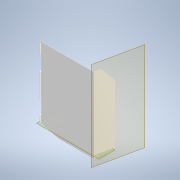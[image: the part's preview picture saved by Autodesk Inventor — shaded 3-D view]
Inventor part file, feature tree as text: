
AUTODESK INVENTOR PART (.ipt)
format: ipt  version: 2021 (Build 250183000, 183)  size: 199,168 bytes
history: native  units: mm
features: sketch x7, extrude x6, fillet x5, plane x2, other x2, hole x1
ambient origin geometry x8: Origin, YZ Plane, XZ Plane, XY Plane, X Axis, Y Axis, Z Axis, Center Point
bodies: Solid1 (feature_tree)
feature tree (23):
  extrude  "Extrusion1"  Depth=1300.0mm
  extrude  "Extrusion2"  Depth=20.0mm
  extrude  "Extrusion3"  Depth=2.5mm
  plane  "Work Plane1"
  extrude  "Extrusion4"  Depth=650.0mm
  fillet  "Fillet1"  Radius=550.0mm
  fillet  "Fillet2"  Radius=200.0mm
  fillet  "Fillet3"  Radius=200.0mm
  plane  "Work Plane2"
  extrude  "Extrusion5"  Depth=1100.0mm TaperAngle=0.0deg
  fillet  "Fillet4"  Radius=1100.0mm
  fillet  "Fillet5"  Radius=309.0mm
  hole  "Hole1"  [1 undecoded]
  extrude  "Extrusion6"  Depth=2.0mm
  sketch  "Sketch1"  dims[d0=925.0mm d1=1300.0mm]
  sketch  "Sketch2"  dims[d2=3.0mm d3=0.0mm d4=20.0mm]
  sketch  "Sketch3"  dims[d5=5.0mm d6=2.5mm]
  sketch  "Sketch4"  dims[d7=1250.0mm d8=0.0mm d9=650.0mm d10=550.0mm d11=200.0mm d12=200.0mm]
  sketch  "Sketch5"  dims[d14=40.0mm d15=30.0mm d16=0.0mm d17=1100.0mm d18=530.0mm d19=309.0mm]
  sketch  "Sketch6"  dims[d20=22.68928mm d21=3.0mm d22=0.0mm]
  sketch  "Sketch7"  dims[d23=6.0mm d24=2.0mm d25=50.0mm d26=1061.7mm d27=-50.0mm d28=18.0mm d29=20.0mm d30=280.0mm d31=10.0mm d32=0.0mm d33=6.0mm d34=6.0mm d35=9.0mm d36=9.0mm d37=8.0mm d38=6.0mm d39=4.0mm d40=2.0mm d41=90.0deg d42=8.0mm d43=20.594885mm d44=40.0mm d45=0.0mm]
  other  "cover_final_assembly.iam"
  other  "wheelchair_box_extended:1"
note: 1 required parameter value undecoded (feature->parameter linkage not recoverable at this tier; creation-order binding heuristic only, values carry confidence <= 0.55)
